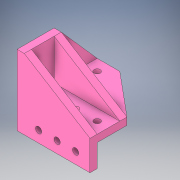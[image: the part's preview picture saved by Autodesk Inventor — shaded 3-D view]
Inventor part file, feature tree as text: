
AUTODESK INVENTOR PART (.ipt)
format: ipt  version: 2019 (Build 230136000, 136)  size: 212,992 bytes
history: native  units: in
note: dims shown in document units (in); Inventor stores cm internally (conversion verified against a paired STEP export)
features: extrude x8, sketch x8, projected_geometry x2, plane x1
ambient origin geometry x8: Origin, YZ Plane, XZ Plane, XY Plane, X Axis, Y Axis, Z Axis, Center Point
bodies: Solid1 (feature_tree)
feature tree (19):
  extrude  "Extrusion1"  Depth=0.7874in
  extrude  "Extrusion2"  Depth=0.25in
  extrude  "Extrusion3"  Depth=2.4528in TaperAngle=0.0deg
  plane  "Work Plane1"
  extrude  "Extrusion4"  Depth=0.7874in
  extrude  "Extrusion5"  Depth=2.4528in TaperAngle=0.0deg
  extrude  "Extrusion7"  Depth=0.3937in
  extrude  "Extrusion8"  Depth=0.3937in
  extrude  "Extrusion9"  [1 undecoded]
  sketch  "Sketch1"  dims[d0=1.5in d1=0.7874in]
  sketch  "Sketch2"  dims[d2=0.7874in d3=0.25in]
  sketch  "Sketch3"  dims[d4=0.25in d5=2.4528in d6=0.0in]
  sketch  "Sketch4"  dims[d7=0.7874in d8=0.2165in]
  projected_geometry  "Projected Loop1"
  sketch  "Sketch5"  dims[d10=1.1811in d12=0.6437in d13=0.3937in d15=1.0in d17=2.4528in d18=0.0in]
  sketch  "Sketch7"  dims[d19=0.3937in d20=0.2165in]
  sketch  "Sketch8"  dims[d21=0.5in d22=1.1811in d24=0.6437in d25=0.3937in d27=1.0in]
  projected_geometry  "Projected Loop2"
  sketch  "Sketch9"  dims[d29=2.4528in d30=0.0in d31=-0.7874in d32=0.7874in d33=1.1811in d35=0.75in d36=0.3937in d38=1.0in d40=0.2165in d41=1.1811in d43=0.75in d44=0.3937in d46=1.0in d48=0.25in d49=0.0in d50=0.25in d51=0.25in d52=0.25in d53=0.0in d59=0.25in d60=0.0in d61=0.25in d62=0.0in d63=0.8327in d64=0.2165in d65=0.25in d66=0.0in d67=0.0in d68=0.5in d69=0.0in]
note: 1 required parameter value undecoded (feature->parameter linkage not recoverable at this tier; creation-order binding heuristic only, values carry confidence <= 0.55)
